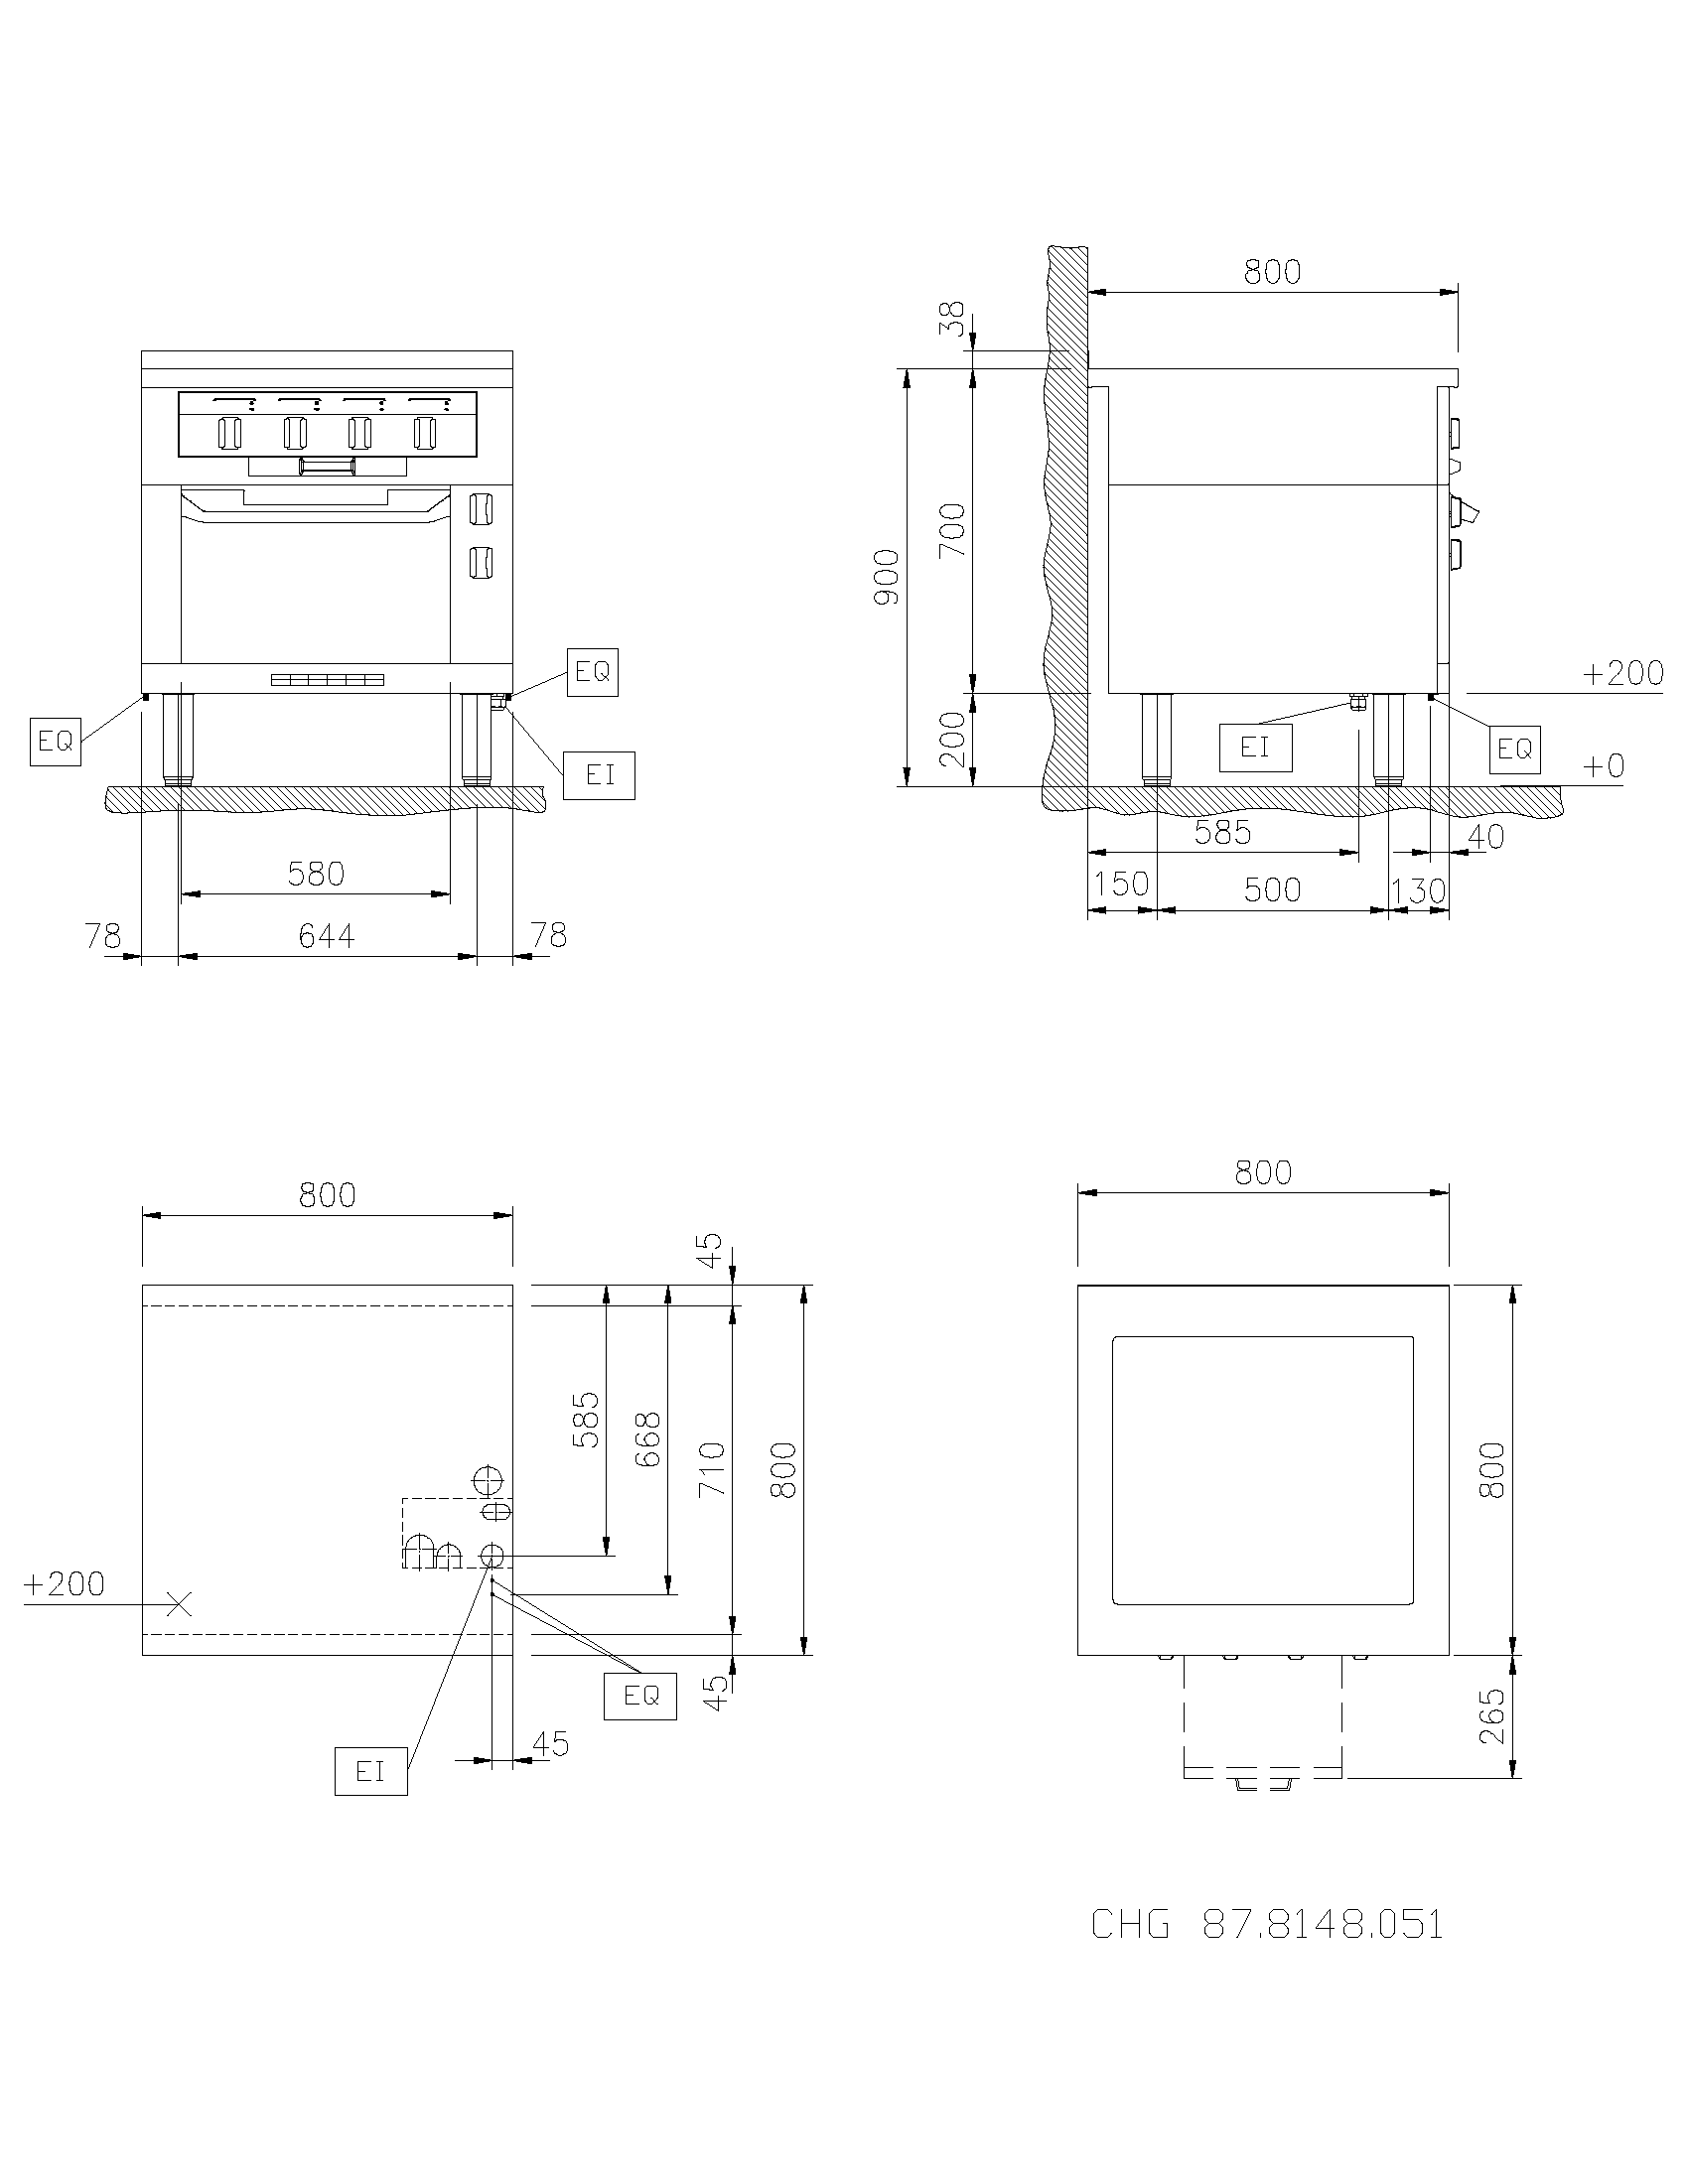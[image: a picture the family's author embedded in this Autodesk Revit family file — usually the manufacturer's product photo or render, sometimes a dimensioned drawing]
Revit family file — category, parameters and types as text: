
# Revit family: QF_ELECTROLUXPROFESSIONAL_588416_MALOECH8AO
name_source: partatom
category: Attrezzature speciali
units: mm (PartAtom-declared; Revit-internal decimal feet)

## family parameters
Basato su piano di lavoro = No
Condiviso = No
Punto di calcolo locali = No
Quota connettore circolare = Usa diametro
Sempre verticale = Sì
Taglio con vuoti quando caricato = No
Tipo di parte = Normale

## types (1)
- Standard
    Accessory = Sì
    Cold Water Size = 0"
    Compressed Air Pressure = 0.00 psi
    Compressed Air Size = 0"
    Compressed Air Volume = 0 GPM
    Condensate Return Size = 0"
    Cycle = 50 Hz
    Depth Actual = 800 mm  [stored 2.62467 ft]
    Descrizione = EL.SOLID T,ECO,ST.OV,PASS,2S,800X800X700
    Direct Waste Size = 0"
    Gas Input Pressure = 0.0
    Gas KW = 0
    Gas Size = 0"
    HP = 23.2 HP
    Height Actual = 700 mm  [stored 2.29659 ft]
    Hot Water Size = 0"
    Item Number = 588416
    Length Actual = 800 mm  [stored 2.62467 ft]
    Modello = MALOECH8AO
    Phase = 3
    Produttore = Electrolux Professional
    Prospetto di default = 0 mm  [stored 0 ft]
    Refrigerant Compressor Remote = Sì
    Refrigeration Liquid Line Size = 0 mm  [stored 0 ft]
    Refrigeration Suction Line Size = 0 mm  [stored 0 ft]
    Steam Consumption per Hour = 0
    Steam Supply Maximum Pressure = 0.00 psi
    Steam Supply Minimum Pressure = 0.00 psi
    Steam Supply Size = 0"
    URL = https://www.electroluxprofessional.com
    URL Manufacturer = https://www.electroluxprofessional.com
    Volts = 400 V
    Watts = 17300 W
    Weight = 211.00 kg

note: source unit labels omitted for Gas Input Pressure — the stored unit's dimension contradicts the parameter name (converter mislabeling)

note: [stored X ft] marks values corroborated as IEEE doubles in the binary element streams (Revit-internal decimal feet)

## geometry (parser evidence)
native form markers: Blend x12, Sweep x17
no freeform markers — native parametric forms only
